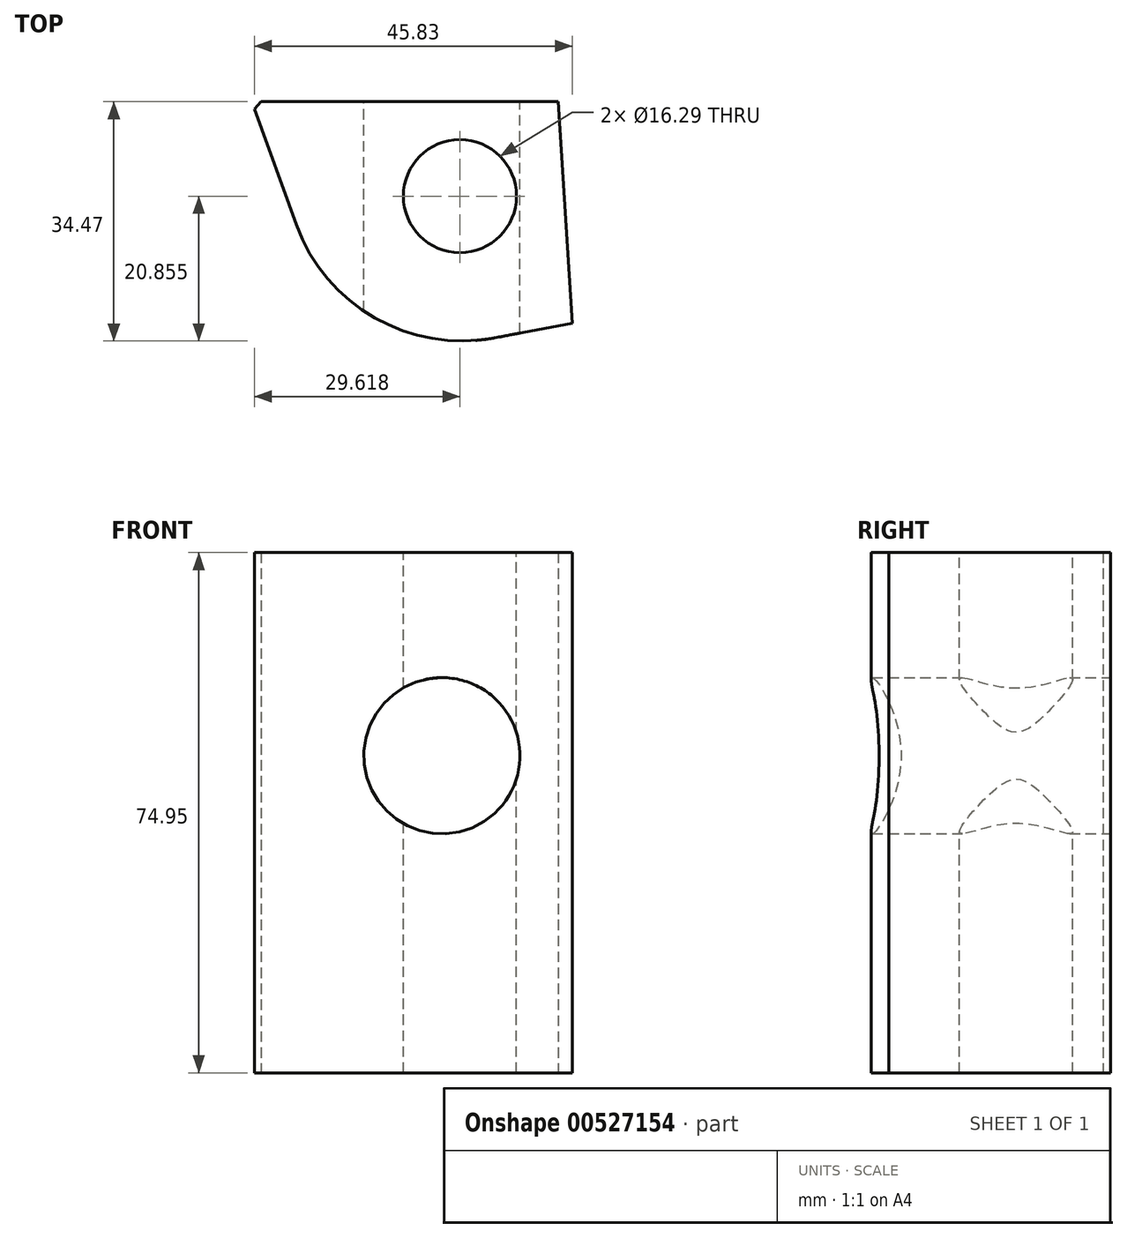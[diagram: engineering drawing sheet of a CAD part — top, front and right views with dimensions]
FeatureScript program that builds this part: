
annotation { "Feature Type Name" : "Feature", "Feature Type Description" : "" }
export const myFeature = defineFeature(function(context is Context, id is Id, definition is map)
    precondition{}
    {
        {
            var Q0;
            Q0=qCreatedBy(makeId("Top.planeOp"),FACE);
            var sketch = newSketch(context, id + "F0", { "sketchPlane" : qUnion([Q0])});
            skLineSegment(sketch, "E0", {"start": v(-16.45, 57.3) * mm, "end": v(26.32, 57.3) * mm});
            skLineSegment(sketch, "E1", {"start": v(26.32, 57.3) * mm, "end": v(28.37, 25.38) * mm});
            skLineSegment(sketch, "E2", {"start": v(28.37, 25.38) * mm, "end": v(-4.05, 19.24) * mm});
            skLineSegment(sketch, "E3", {"start": v(-4.05, 19.24) * mm, "end": v(-17.46, 56.22) * mm});
            skLineSegment(sketch, "E4", {"start": v(-17.46, 56.22) * mm, "end": v(-16.45, 57.3) * mm});
            skSolve(sketch);
        }
        {
            var Q0;
            Q0=makeQuery(id+"F0.imprint","IMPRINT",FACE,{"disambiguationData":[TD([[makeQuery(id+"F0.imprint","IMPRINT",EDGE,{"derivedFrom":sQuery(id+"F0.wireOp",EDGE,"E0")}),-1.0]])]});
            extrude(context, id + "F1", {"entities" : qUnion([Q0]), "depth" : 74.95 * mm, "offsetDistance" : 25.4 * mm});
        }
        {
            var Q0;
            Q0=makeQuery(id+"F1.opExtrude","CAP_FACE",FACE,{"disambiguationData":[OSD([sQuery(id+"F0.wireOp",EDGE,"E0"),sQuery(id+"F0.wireOp",EDGE,"E1"),sQuery(id+"F0.wireOp",EDGE,"E2"),sQuery(id+"F0.wireOp",EDGE,"E3"),sQuery(id+"F0.wireOp",EDGE,"E4")])],"isStart":false});
            var sketch = newSketch(context, id + "F2", { "sketchPlane" : qUnion([Q0])});
            skCircle(sketch, "E5", {"center": v(12.16, 43.68) * mm, "radius": 8.14 * mm});
            skPoint(sketch, "E5.centerSnap0", {"position": v(12.16, 22.3) * mm});
            skSolve(sketch);
        }
        {
            var Q0;
            Q0 = qSketchRegion(id + "F2", true);
            extrude(context, id + "F3", {"entities" : qUnion([Q0]), "operationType" : NewBodyOperationType.REMOVE, "oppositeDirection" : true, "depth" : 124.3 * mm, "offsetDistance" : 25.4 * mm});
        }
        {
            var Q0;
            Q0=makeQuery(id+"F1.opExtrude","SWEPT_FACE",FACE,{"disambiguationData":[OSD([sQuery(id+"F0.wireOp",EDGE,"E0")])]});
            var sketch = newSketch(context, id + "F4", { "sketchPlane" : qUnion([Q0])});
            skSolve(sketch);
        }
        {
            var Q0;
            {var subQ0=sQuery(id+"F0.wireOp",EDGE,"E0");Q0=makeQuery(id+"F4.imprint","IMPRINT",FACE,{"disambiguationData":[TD([[makeQuery(id+"F4.imprint","IMPRINT",EDGE,{"derivedFrom":makeQuery(id+"F1.opExtrude","CAP_EDGE",EDGE,{"disambiguationData":[OSD([subQ0])],"isStart":true})}),-1.0]])]});}
            var sketch = newSketch(context, id + "F5", { "sketchPlane" : qUnion([Q0])});
            skCircle(sketch, "E6", {"center": v(-9.57, 45.68) * mm, "radius": 11.25 * mm});
            skSolve(sketch);
        }
        {
            var Q0;
            Q0=makeQuery(id+"F5.imprint","IMPRINT",FACE,{"disambiguationData":[TD([[makeQuery(id+"F5.imprint","IMPRINT",EDGE,{"derivedFrom":sQuery(id+"F5.wireOp",EDGE,"E6")}),1.0]])]});
            extrude(context, id + "F6", {"entities" : qUnion([Q0]), "operationType" : NewBodyOperationType.REMOVE, "endBound" : BoundingType.THROUGH_ALL, "oppositeDirection" : true, "depth" : 25.4 * mm, "offsetDistance" : 25.4 * mm});
        }
        {
            var Q0;
            Q0=makeQuery(id+"F1.opExtrude","SWEPT_EDGE",EDGE,{"disambiguationData":[OSD([sQuery(id+"F0.wireOp",EDGE,"E2"),sQuery(id+"F0.wireOp",EDGE,"E3")])]});
            fillet(context, id + "F7", {"entities" : qUnion([Q0]), "radius" : 25.4 * mm, "tangentPropagation" : true, "allowEdgeOverflow" : false});
        }
    });
